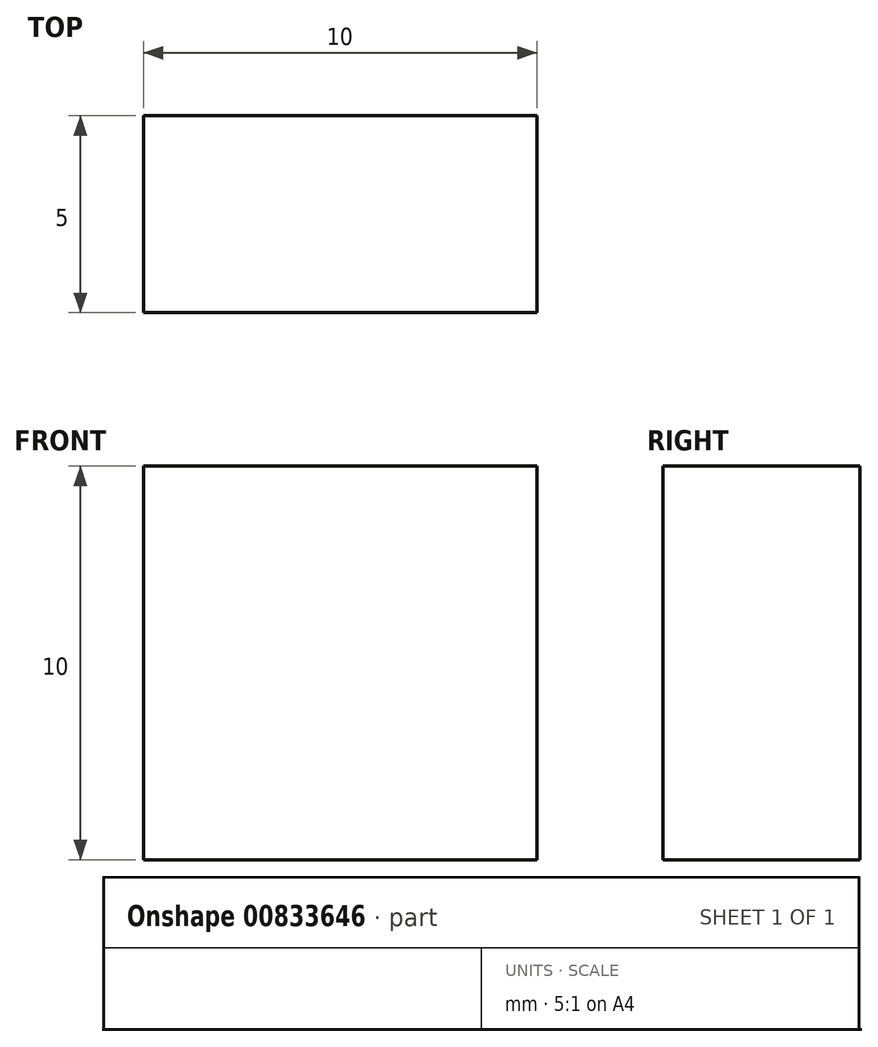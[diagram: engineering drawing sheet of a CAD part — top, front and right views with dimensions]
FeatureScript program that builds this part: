
annotation { "Feature Type Name" : "Feature", "Feature Type Description" : "" }
export const myFeature = defineFeature(function(context is Context, id is Id, definition is map)
    precondition{}
    {
        {
            var Q0;
            Q0=qCreatedBy(makeId("Front.planeOp"),FACE);
            var sketch = newSketch(context, id + "F0", { "sketchPlane" : qUnion([Q0])});
            skLineSegment(sketch, "E0.bottom", {"start": v(-5, 5) * mm, "end": v(5, 5) * mm});
            skLineSegment(sketch, "E0.top", {"start": v(-5, -5) * mm, "end": v(5, -5) * mm});
            skLineSegment(sketch, "E0.left", {"start": v(-5, 5) * mm, "end": v(-5, -5) * mm});
            skLineSegment(sketch, "E0.right", {"start": v(5, 5) * mm, "end": v(5, -5) * mm});
            skPoint(sketch, "E0.middle", {"position": v(0, 0) * mm});
            skSolve(sketch);
        }
        {
            var Q0;
            Q0 = qSketchRegion(id + "F0", true);
            extrude(context, id + "F1", {"entities" : qUnion([Q0]), "depth" : 5 * mm, "offsetDistance" : 25 * mm});
        }
    });
